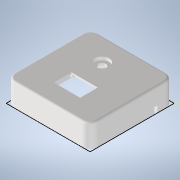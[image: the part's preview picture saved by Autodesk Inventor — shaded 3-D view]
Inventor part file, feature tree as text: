
AUTODESK INVENTOR PART (.ipt)
format: ipt  version: 2022.2 (Build 262287000, 287)  size: 290,304 bytes
history: native  units: mm
features: extrude x15, sketch x15, reference x5, other x4, fillet x2, projected_geometry x1
ambient origin geometry x8: Origin, YZ Plane, XZ Plane, XY Plane, X Axis, Y Axis, Z Axis, Center Point
bodies: Volumenkörper1 (feature_tree)
feature tree (42):
  extrude  "Extrusion1"  Depth=60.6mm
  sketch  "Skizze2"  dims[d2=54.2mm d3=19.3mm]
  extrude  "Extrusion3"  Depth=54.2mm
  extrude  "Extrusion4"  Depth=81.0mm
  extrude  "Extrusion5"  Depth=18.0mm
  extrude  "Extrusion6"  Depth=12.0mm
  extrude  "Extrusion7"  Depth=50.0mm
  extrude  "Extrusion8"  Depth=2.0mm TaperAngle=0.0deg
  fillet  "Rundung1"  Radius=25.4mm
  fillet  "Rundung2"  Radius=17.0mm
  extrude  "Extrusion9"  Depth=2.0mm
  extrude  "Extrusion10"  Depth=2.0mm
  extrude  "Extrusion11"  Depth=1.0mm TaperAngle=0.0deg
  extrude  "Extrusion12"  Depth=0.5mm
  extrude  "Extrusion13"  Depth=5.0mm
  extrude  "Extrusion14"  Depth=1.0mm
  extrude  "Extrusion15"  Depth=1.0mm
  extrude  "Extrusion16"  Depth=16.0mm TaperAngle=0.0deg
  sketch  "Skizze1"  dims[d0=30.3mm d1=60.6mm]
  sketch  "Skizze3"  dims[d4=81.0mm d5=81.0mm]
  sketch  "Skizze4"  dims[d6=40.5mm d7=18.0mm]
  sketch  "Skizze5"  dims[d8=20.0mm d9=0.0mm d12=12.0mm]
  sketch  "Skizze6"  dims[d13=50.0mm d14=25.0mm]
  sketch  "Skizze7"  dims[d15=20.0mm d16=0.0mm d17=2.0mm d18=0.0mm d19=25.4mm d20=17.0mm]
  sketch  "Skizze8"  dims[d21=12.7mm d22=2.0mm]
  sketch  "Skizze9"  dims[d23=20.0mm d24=0.0mm d25=2.0mm]
  reference  "Referenz1"
  reference  "Referenz2"
  reference  "Referenz3"
  sketch  "Skizze10"  dims[d26=2.0mm d27=1.0mm d28=0.0mm]
  reference  "Referenz4"
  reference  "Referenz5"
  sketch  "Skizze11"  dims[d29=4.0mm d30=0.5mm]
  projected_geometry  "Projizierte Kontur1"
  sketch  "Skizze12"  dims[d31=5.0mm d32=5.0mm]
  sketch  "Skizze14"  dims[d33=0.5mm d34=1.0mm]
  sketch  "Skizze15"  dims[d35=2.5mm d36=0.0mm d37=1.0mm]
  sketch  "Skizze16"  dims[d38=1.4mm d39=29.5mm d40=0.0mm d41=8.0mm d42=2.0mm d43=2.5mm d44=0.0mm d45=11.0mm d46=9.0mm d47=3.0mm d48=10.0mm d49=0.0mm d50=10.0mm d51=0.0mm d52=14.0mm d53=24.0mm d54=7.5mm d55=10.0mm d56=0.0mm d57=18.0mm d58=3.0mm d59=0.0mm d60=0.0mm d61=0.0mm d62=14.0mm d63=3.0mm d64=0.0mm d65=6.0mm d66=3.0mm d67=16.0mm d68=27.75mm d69=0.0mm d70=9.5mm]
  parser-record x1  (decoder bookkeeping rows leaked as tree rows — omitted from the tree; the rows remain in map.json)
  other  "Zusammenbau.iam"
  other  "ClipUnten:1"
  other  "Clip:1"
note: 1 file-system path scrubbed to <path> (originals preserved in map.json)
